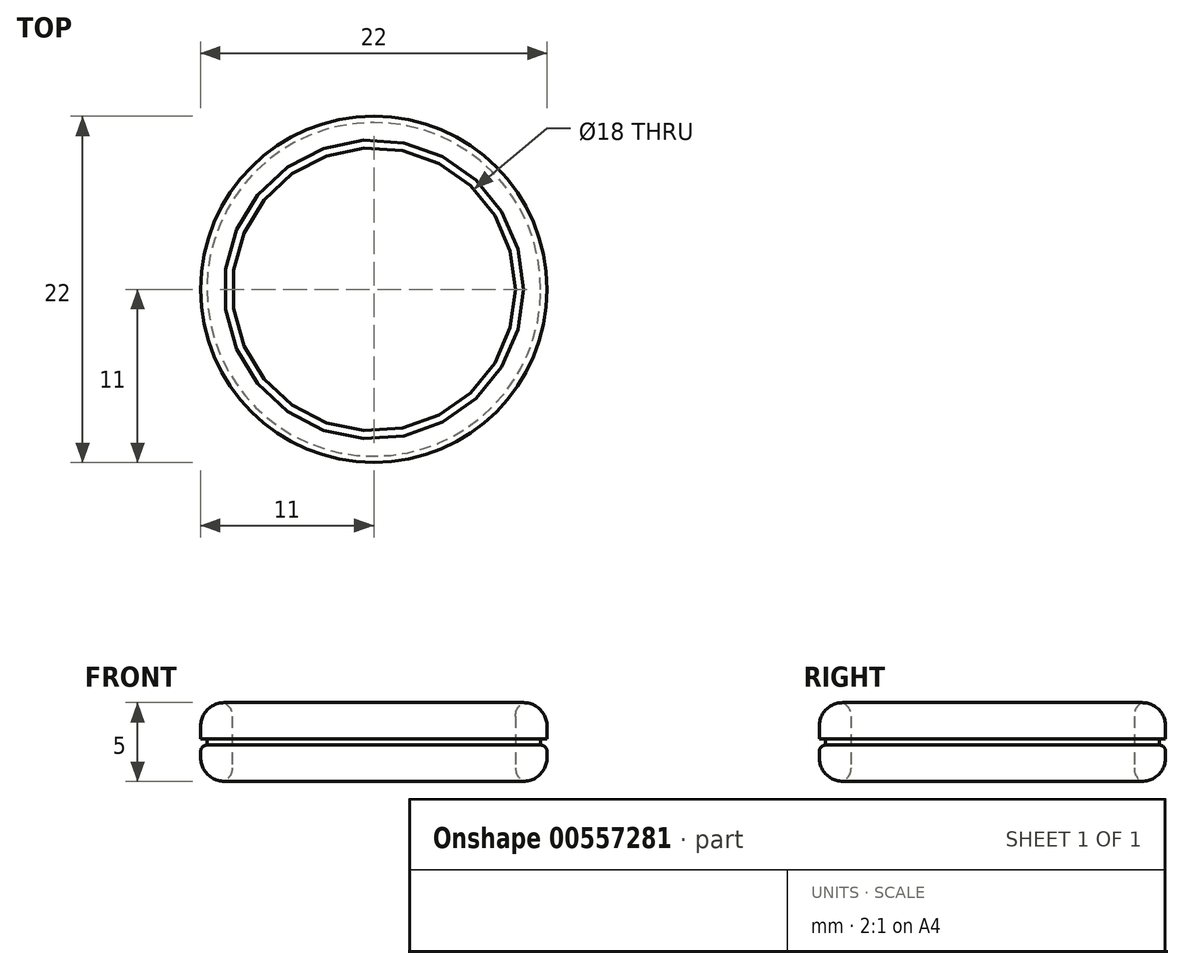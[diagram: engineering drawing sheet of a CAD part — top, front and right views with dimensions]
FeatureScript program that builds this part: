
annotation { "Feature Type Name" : "Feature", "Feature Type Description" : "" }
export const myFeature = defineFeature(function(context is Context, id is Id, definition is map)
    precondition{}
    {
        {
            var Q0;
            Q0=qCreatedBy(makeId("Top.planeOp"),FACE);
            var sketch = newSketch(context, id + "F0", { "sketchPlane" : qUnion([Q0])});
            skCircle(sketch, "E0", {"center": v(0, 0) * mm, "radius": 9 * mm});
            skCircle(sketch, "E1", {"center": v(0, 0) * mm, "radius": 11 * mm});
            skSolve(sketch);
        }
        {
            var Q0;
            Q0 = qSketchRegion(id + "F0", true);
            extrude(context, id + "F1", {"entities" : qUnion([Q0]), "endBound" : BoundingType.SYMMETRIC, "depth" : 5 * mm, "offsetDistance" : 25 * mm});
        }
        {
            var Q0;
            Q0=makeQuery(id+"F1.opExtrude","CAP_EDGE",EDGE,{"disambiguationData":[OSD([sQuery(id+"F0.wireOp",EDGE,"E1")])],"isStart":false});
            var Q1;
            Q1=makeQuery(id+"F1.opExtrude","CAP_EDGE",EDGE,{"disambiguationData":[OSD([sQuery(id+"F0.wireOp",EDGE,"E1")])],"isStart":true});
            fillet(context, id + "F2", {"entities" : qUnion([Q0, Q1]), "radius" : 1.5 * mm, "tangentPropagation" : true, "allowEdgeOverflow" : false});
        }
        {
            var Q0;
            Q0=makeQuery(id+"F1.opExtrude","CAP_EDGE",EDGE,{"disambiguationData":[OSD([sQuery(id+"F0.wireOp",EDGE,"E0")])],"isStart":false});
            var Q1;
            Q1=makeQuery(id+"F1.opExtrude","CAP_EDGE",EDGE,{"disambiguationData":[OSD([sQuery(id+"F0.wireOp",EDGE,"E0")])],"isStart":true});
            fillet(context, id + "F3", {"entities" : qUnion([Q0, Q1]), "radius" : 1 * mm, "tangentPropagation" : true, "rho" : 0.5, "crossSection" : FilletCrossSection.CONIC, "allowEdgeOverflow" : false});
        }
        {
            var Q0;
            Q0=qCreatedBy(makeId("Top.planeOp"),FACE);
            var sketch = newSketch(context, id + "F4", { "sketchPlane" : qUnion([Q0])});
            skCircle(sketch, "E2", {"center": v(0, 0) * mm, "radius": 11 * mm});
            skCircle(sketch, "E3", {"center": v(0, 0) * mm, "radius": 10.6 * mm});
            skSolve(sketch);
        }
        {
            var Q0;
            Q0 = qSketchRegion(id + "F4", true);
            extrude(context, id + "F5", {"entities" : qUnion([Q0]), "operationType" : NewBodyOperationType.REMOVE, "endBound" : BoundingType.SYMMETRIC, "depth" : 0.4 * mm, "offsetDistance" : 25 * mm});
        }
        {
            var Q0;
            Q0=makeQuery(id+"F5.boolean.opBoolean","COPY",EDGE,{"derivedFrom":makeQuery(id+"F5.opExtrude","CAP_EDGE",EDGE,{"disambiguationData":[OSD([sQuery(id+"F4.wireOp",EDGE,"E2")])],"isStart":false})});
            var Q1;
            Q1=makeQuery(id+"F5.boolean.opBoolean","COPY",EDGE,{"derivedFrom":makeQuery(id+"F5.opExtrude","CAP_EDGE",EDGE,{"disambiguationData":[OSD([sQuery(id+"F4.wireOp",EDGE,"E2")])],"isStart":true})});
            fillet(context, id + "F6", {"entities" : qUnion([Q0, Q1]), "radius" : 0.4 * mm, "tangentPropagation" : true, "allowEdgeOverflow" : false});
        }
    });
